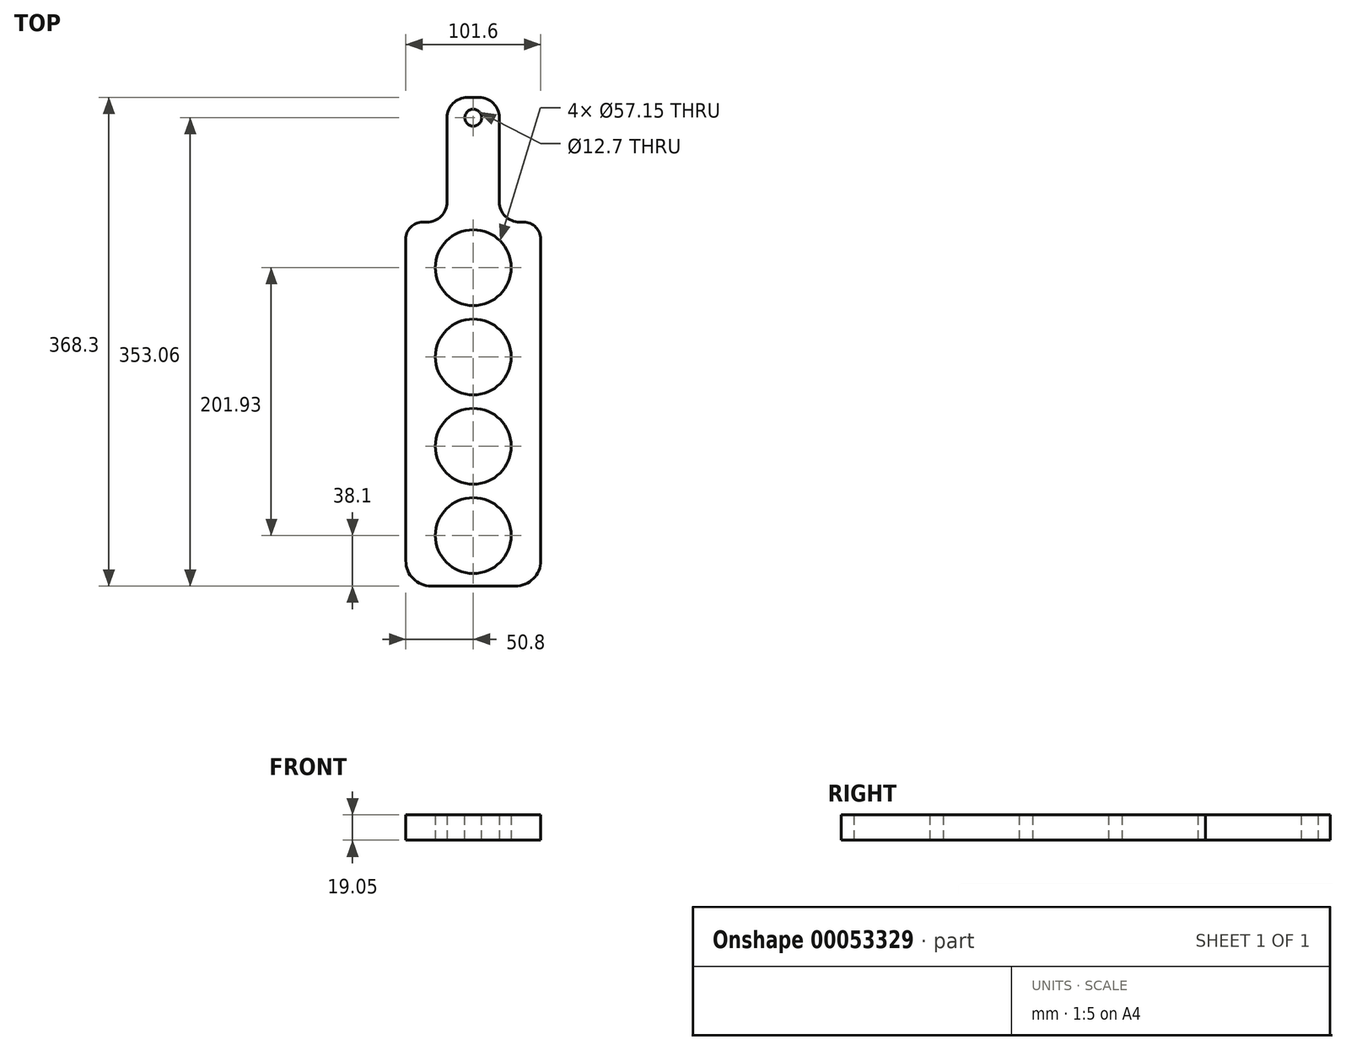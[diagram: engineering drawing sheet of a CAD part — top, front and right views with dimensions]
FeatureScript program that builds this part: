
annotation { "Feature Type Name" : "Feature", "Feature Type Description" : "" }
export const myFeature = defineFeature(function(context is Context, id is Id, definition is map)
    precondition{}
    {
        {
            var Q0;
            Q0=qCreatedBy(makeId("Top.planeOp"),FACE);
            var sketch = newSketch(context, id + "F0", { "sketchPlane" : qUnion([Q0])});
            skLineSegment(sketch, "E0.rect.bottom", {"start": v(-31.75, -184.15) * mm, "end": v(31.75, -184.15) * mm});
            skLineSegment(sketch, "E0.rect.top", {"start": v(-4.45, 184.15) * mm, "end": v(4.45, 184.15) * mm});
            skLineSegment(sketch, "E0.rect.left", {"start": v(-50.8, -165.1) * mm, "end": v(-50.8, 77.47) * mm});
            skLineSegment(sketch, "E0.rect.right", {"start": v(50.8, -165.1) * mm, "end": v(50.8, 77.47) * mm});
            skPoint(sketch, "E0.rect.middle", {"position": v(0, 0) * mm});
            skLineSegment(sketch, "E1", {"start": v(0, 218.03) * mm, "end": v(0, -200.06) * mm, "construction": true});
            skCircle(sketch, "E2", {"center": v(0, -146.05) * mm, "radius": 28.58 * mm});
            skCircle(sketch, "E3", {"center": v(0, -78.74) * mm, "radius": 28.58 * mm});
            skCircle(sketch, "E4", {"center": v(0, -11.43) * mm, "radius": 28.58 * mm});
            skCircle(sketch, "E5", {"center": v(0, 55.88) * mm, "radius": 28.58 * mm});
            skLineSegment(sketch, "E6", {"start": v(-38.1, 90.17) * mm, "end": v(-34.93, 90.17) * mm});
            skLineSegment(sketch, "E7", {"start": v(-19.69, 105.41) * mm, "end": v(-19.69, 168.9) * mm});
            skPoint(sketch, "E8.orphan", {"position": v(-50.8, 184.15) * mm});
            skLineSegment(sketch, "E9", {"start": v(19.69, 168.9) * mm, "end": v(19.69, 105.41) * mm});
            skLineSegment(sketch, "E10", {"start": v(34.93, 90.17) * mm, "end": v(38.1, 90.17) * mm});
            skPoint(sketch, "E11.orphan", {"position": v(50.8, 184.15) * mm});
            skPoint(sketch, "E12.visualSharp", {"position": v(-19.69, 90.17) * mm});
            skArc(sketch, "E12.filletArc", {"start": v(-34.93, 90.17) * mm, "mid": v(-24.15, 94.63) * mm, "end": v(-19.69, 105.41) * mm});
            skPoint(sketch, "E13.visualSharp", {"position": v(19.69, 90.17) * mm});
            skArc(sketch, "E13.filletArc", {"start": v(19.69, 105.41) * mm, "mid": v(24.15, 94.63) * mm, "end": v(34.93, 90.17) * mm});
            skPoint(sketch, "E14.visualSharp", {"position": v(-19.69, 184.15) * mm});
            skArc(sketch, "E14.filletArc", {"start": v(-4.45, 184.15) * mm, "mid": v(-15.22, 179.69) * mm, "end": v(-19.69, 168.9) * mm});
            skPoint(sketch, "E15.visualSharp", {"position": v(19.69, 184.15) * mm});
            skArc(sketch, "E15.filletArc", {"start": v(19.69, 168.9) * mm, "mid": v(15.22, 179.69) * mm, "end": v(4.45, 184.15) * mm});
            skPoint(sketch, "E16.visualSharp", {"position": v(-50.8, -184.15) * mm});
            skArc(sketch, "E16.filletArc", {"start": v(-50.8, -165.1) * mm, "mid": v(-45.22, -178.57) * mm, "end": v(-31.75, -184.15) * mm});
            skPoint(sketch, "E17.visualSharp", {"position": v(50.8, -184.15) * mm});
            skArc(sketch, "E17.filletArc", {"start": v(31.75, -184.15) * mm, "mid": v(45.22, -178.57) * mm, "end": v(50.8, -165.1) * mm});
            skPoint(sketch, "E18.visualSharp", {"position": v(-50.8, 90.17) * mm});
            skArc(sketch, "E18.filletArc", {"start": v(-38.1, 90.17) * mm, "mid": v(-47.08, 86.45) * mm, "end": v(-50.8, 77.47) * mm});
            skPoint(sketch, "E19.visualSharp", {"position": v(50.8, 90.17) * mm});
            skArc(sketch, "E19.filletArc", {"start": v(50.8, 77.47) * mm, "mid": v(47.08, 86.45) * mm, "end": v(38.1, 90.17) * mm});
            skSolve(sketch);
        }
        {
            var Q0;
            Q0 = qSketchRegion(id + "F0", true);
            extrude(context, id + "F1", {"entities" : qUnion([Q0]), "depth" : 19.05 * mm});
        }
        {
            var Q0;
            Q0=makeQuery(id+"F1.opExtrude","CAP_FACE",FACE,{"disambiguationData":[OSD([sQuery(id+"F0.wireOp",EDGE,"E0.rect.bottom"),sQuery(id+"F0.wireOp",EDGE,"E0.rect.top"),sQuery(id+"F0.wireOp",EDGE,"E0.rect.left"),sQuery(id+"F0.wireOp",EDGE,"E0.rect.right"),sQuery(id+"F0.wireOp",EDGE,"E2"),sQuery(id+"F0.wireOp",EDGE,"E3"),sQuery(id+"F0.wireOp",EDGE,"E4"),sQuery(id+"F0.wireOp",EDGE,"E5"),sQuery(id+"F0.wireOp",EDGE,"E6"),sQuery(id+"F0.wireOp",EDGE,"E7"),sQuery(id+"F0.wireOp",EDGE,"E9"),sQuery(id+"F0.wireOp",EDGE,"E10"),sQuery(id+"F0.wireOp",EDGE,"E12.filletArc"),sQuery(id+"F0.wireOp",EDGE,"E13.filletArc"),sQuery(id+"F0.wireOp",EDGE,"E14.filletArc"),sQuery(id+"F0.wireOp",EDGE,"E15.filletArc"),sQuery(id+"F0.wireOp",EDGE,"E16.filletArc"),sQuery(id+"F0.wireOp",EDGE,"E17.filletArc"),sQuery(id+"F0.wireOp",EDGE,"E18.filletArc"),sQuery(id+"F0.wireOp",EDGE,"E19.filletArc")])],"isStart":false});
            var sketch = newSketch(context, id + "F2", { "sketchPlane" : qUnion([Q0])});
            skCircle(sketch, "E20", {"center": v(0, 168.9) * mm, "radius": 6.35 * mm});
            skPoint(sketch, "E21.0", {"position": v(-4.45, 184.15) * mm});
            skSolve(sketch);
        }
        {
            var Q0;
            Q0 = qSketchRegion(id + "F2", true);
            extrude(context, id + "F3", {"entities" : qUnion([Q0]), "operationType" : NewBodyOperationType.REMOVE, "endBound" : BoundingType.THROUGH_ALL, "oppositeDirection" : true, "depth" : 25.4 * mm});
        }
    });
